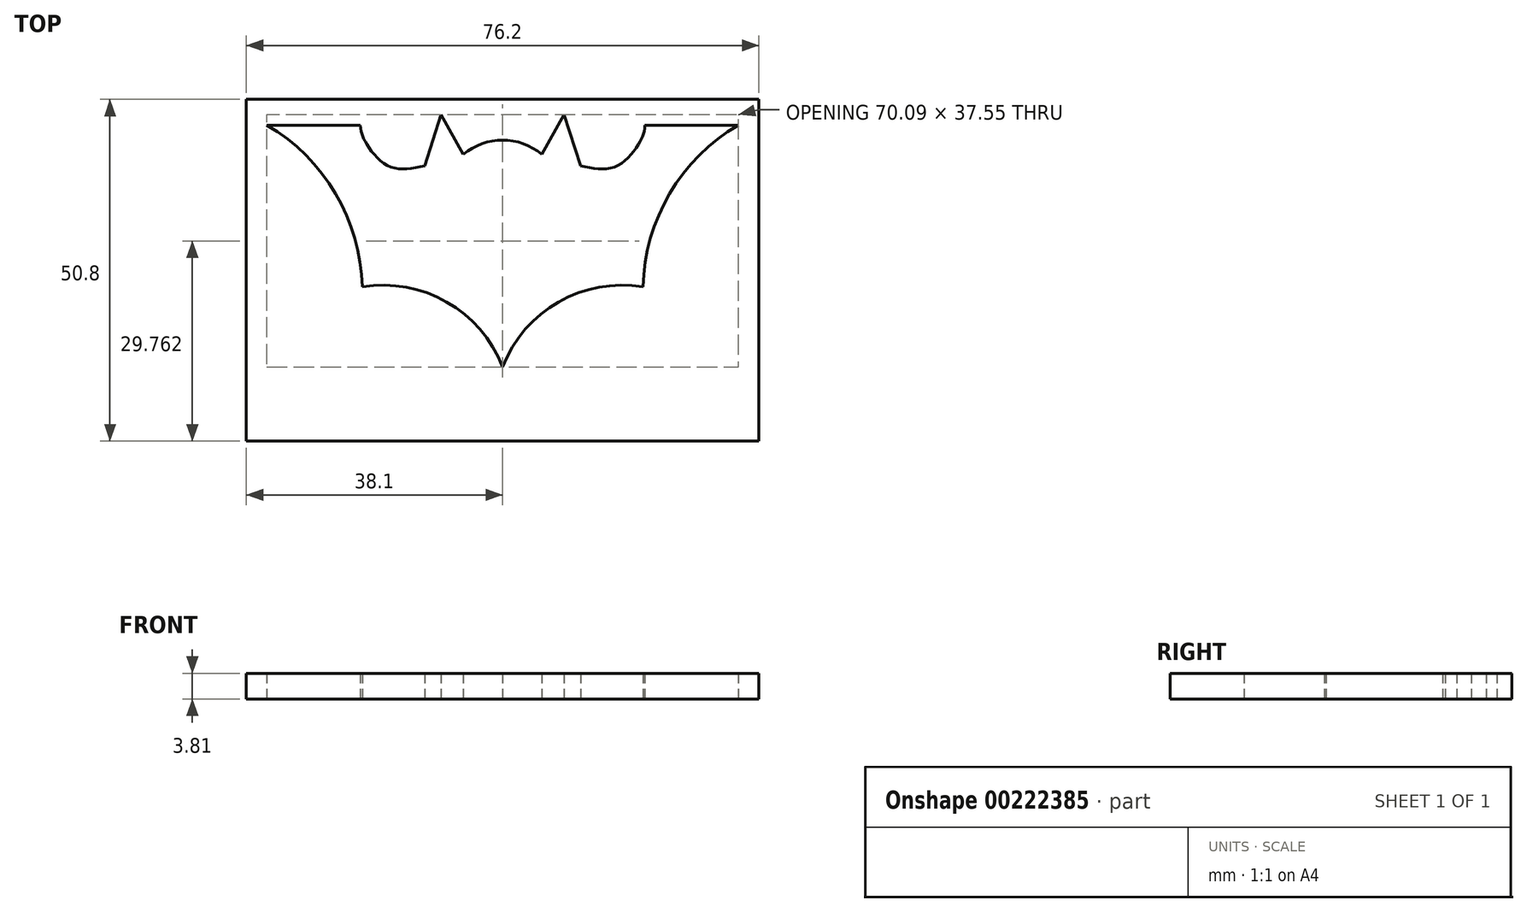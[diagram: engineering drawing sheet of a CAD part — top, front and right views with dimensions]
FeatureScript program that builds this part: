
annotation { "Feature Type Name" : "Feature", "Feature Type Description" : "" }
export const myFeature = defineFeature(function(context is Context, id is Id, definition is map)
    precondition{}
    {
        {
            var Q0;
            Q0=qCreatedBy(makeId("Top.planeOp"),FACE);
            var sketch = newSketch(context, id + "F0", { "sketchPlane" : qUnion([Q0])});
            skLineSegment(sketch, "E0.bottom", {"start": v(0, 0) * mm, "end": v(76.2, 0) * mm});
            skLineSegment(sketch, "E0.top", {"start": v(0, -50.8) * mm, "end": v(76.2, -50.8) * mm});
            skLineSegment(sketch, "E0.left", {"start": v(0, 0) * mm, "end": v(0, -50.8) * mm});
            skLineSegment(sketch, "E0.right", {"start": v(76.2, 0) * mm, "end": v(76.2, -50.8) * mm});
            skPoint(sketch, "E1.centerSnap0", {"position": v(38.1, -50.8) * mm});
            skLineSegment(sketch, "E2", {"start": v(38.1, -50.8) * mm, "end": v(38.1, 0) * mm, "construction": true});
            skArc(sketch, "E3", {"start": v(38.1, -6.07) * mm, "mid": v(35, -6.61) * mm, "end": v(32.27, -8.2) * mm});
            skLineSegment(sketch, "E4", {"start": v(32.27, -8.2) * mm, "end": v(28.96, -2.27) * mm});
            skLineSegment(sketch, "E5", {"start": v(28.96, -2.27) * mm, "end": v(26.52, -9.91) * mm});
            skFitSpline(sketch, "E6", {"points": [v(26.52, -9.91) * mm, v(21.13, -9.91) * mm, v(17.66, -6.26) * mm, v(16.96, -3.83) * mm], "startDerivative": vector(-15.88, -2.75) * mm, "endDerivative": vector(-0.74, 12.09) * mm});
            skLineSegment(sketch, "E7", {"start": v(16.96, -3.83) * mm, "end": v(3.06, -3.83) * mm});
            skArc(sketch, "E8", {"start": v(17.23, -27.89) * mm, "mid": v(13.27, -14.02) * mm, "end": v(3.06, -3.83) * mm});
            skArc(sketch, "E9", {"start": v(38.1, -39.81) * mm, "mid": v(29.8, -30.12) * mm, "end": v(17.23, -27.89) * mm});
            skArc(sketch, "E10.MirrorCS", {"start": v(38.1, -6.07) * mm, "mid": v(41.2, -6.61) * mm, "end": v(43.93, -8.2) * mm});
            skLineSegment(sketch, "E11.MirrorCS", {"start": v(43.93, -8.2) * mm, "end": v(47.24, -2.27) * mm});
            skLineSegment(sketch, "E12.MirrorCS", {"start": v(47.24, -2.27) * mm, "end": v(49.68, -9.91) * mm});
            skFitSpline(sketch, "E13.MirrorCS", {"points": [v(49.68, -9.91) * mm, v(55.07, -9.91) * mm, v(58.54, -6.26) * mm, v(59.24, -3.83) * mm], "startDerivative": vector(15.88, -2.75) * mm, "endDerivative": vector(0.74, 12.09) * mm});
            skLineSegment(sketch, "E14.MirrorCS", {"start": v(59.24, -3.83) * mm, "end": v(73.14, -3.83) * mm});
            skArc(sketch, "E15.MirrorCS", {"start": v(58.97, -27.89) * mm, "mid": v(62.93, -14.02) * mm, "end": v(73.14, -3.83) * mm});
            skArc(sketch, "E16.MirrorCS", {"start": v(38.1, -39.81) * mm, "mid": v(46.4, -30.12) * mm, "end": v(58.97, -27.89) * mm});
            skSolve(sketch);
        }
        {
            var Q0;
            Q0=makeQuery(id+"F0.imprint","IMPRINT",FACE,{"disambiguationData":[TD([[makeQuery(id+"F0.imprint","IMPRINT",EDGE,{"derivedFrom":sQuery(id+"F0.wireOp",EDGE,"E0.bottom")}),-1.0]])]});
            extrude(context, id + "F1", {"entities" : qUnion([Q0]), "depth" : 3.8 * mm});
        }
    });
